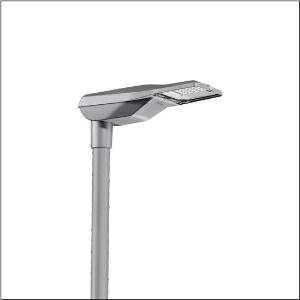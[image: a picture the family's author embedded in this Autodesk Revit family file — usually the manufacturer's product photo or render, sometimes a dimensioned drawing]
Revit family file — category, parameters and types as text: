
# Revit family: streetlight_sl_21_iq_micro___st0_8a_5xe1c31g08cb_6ed2
name_source: partatom
category: Lighting Fixtures
units: mm (PartAtom-declared; Revit-internal decimal feet)

## family parameters
Cut with Voids When Loaded = No
Host = Face
Light Source = No
Part Type = Normal
Room Calculation Point = No
Round Connector Dimension = Use Diameter
Shared = No

## types (1)
- --- (1 x LED, 2870 lm, 19.4 W, 3000K)
    Apparent Load = 19 VA
    CIE Flux Codes = 38 75 97 100 100
    Color Rendering = 70
    Color Temperature = 3000K
    Default Elevation = 1800 mm
    Description = Streetlight SL 21 iQ micro, mast luminaire, primary light control with lens, of PMMA, primary optical cover: cover, of toughened safety glass, transparent, light distribution: ST0.8a, light emission: direct distribution, primary light characteristic: asymmetric, installation type: post-top, side-entry, LED, High Power LED, rated luminous flux: 2.870lm, luminous efficacy: 148lm/W, light colour: 730, colour temperature: 3000K, control: Street-Remote, Auto-Match, Temp-Guard, Lumen-Switch, Night-Set, Smart-Wire, Light-Fading, Desk-Remote (wireless, voltage-free reading and setting of iQ features in the workshop via application-optimized NFC function/RFID function), optimised constant luminous flux control (CLO 2.0), presetting dimming linear, mains connection: 220..240V, AC, 50/60Hz, start of lifetime: 19W, end of service life: 20W, reduction: 10W, luminaire housing, of diecast aluminium, powder-coated, Siteco® metallic grey (DB 702S), corrosivity category C5 mid according to DIN EN ISO 12944, please order mast flange separately, inclination adjustable: 0°, 5°, 10°, 15°, sealing non-destructively replaceable, multi-level sealing system, length: 528mm, width: 235mm, height: 110mm, mast flange for spigot size: 42mm (side-entry): 5XC10008XM4, 60/48mm (side-entry/post-top): 5XC10108XM2, 76/60mm (side-entry/post-top): 5XC10108XM1, protection rating (complete): IP66, insulation class (complete): insulation class II (safety insulation), certification: CE, ENEC, ENEC+, VDE, impact resistance: IK09, permissible operating ambient temperature for outdoor applications: -40..+50°C, standard-compliant lighting for roads and squares, packaging unit: 1 piece

Light Distribution: ST0.8a
    Height = 110 mm
    Lamp = 1 x LED
    Lamp Light Flux = 2870 lm
    Lamp Power = 19.4 W
    Lamp count = 1
    Length = 528 mm
    Luminous efficacy = 148 lm/W
    Manufacturer = Siteco
    ModVariant = No
    Model = 5XE1C31G08CB
    Number of Poles = 1
    OnlyDefault = Yes
    Power Factor = 1
    Product Name = Streetlight SL 21 iQ micro | ST0.8a
    Product group = mast luminaire | pylon top
    ProductGroupID = 6100
    Protection Class = Protection class II
    Protection Degree = IP 66
    RLX_Detail_Level = 1
    RLX_Emergency_Light_Flux = 0 lm
    RLX_Emergency_Type = 0
    RLX_Emergency_Type_DB = No
    RlxData = <blob elided: 98633 chars, md5=e8a5658e>
    Socket = socket
    Standby Power = 0 W
    System Light Flux = 2870 lm
    System Power = 19 W
    Type Comments = factory setting: luminous flux: 100 % | dim-lin: 254 | 387 mA
    Type Image = l_1006881.jpg
    URL = http://relux.com
    VarID = @adj_087797
    Voltage = 0 V
    Weight = 0.00 kg
    Width = 235 mm

## geometry (parser evidence)
native form markers: Blend x4, Sweep x10
no freeform markers — native parametric forms only
